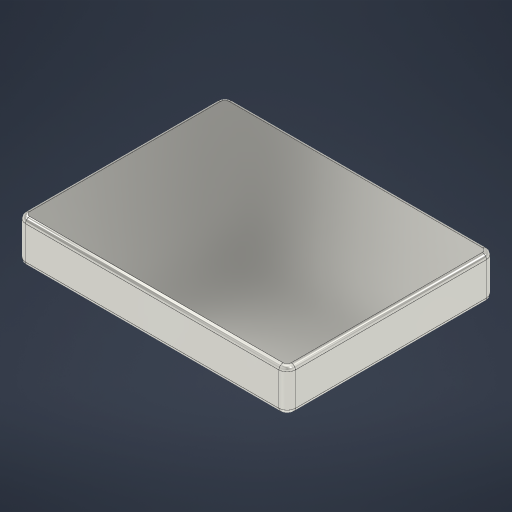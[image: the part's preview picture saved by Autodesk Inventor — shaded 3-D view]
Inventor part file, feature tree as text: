
AUTODESK INVENTOR PART (.ipt)
format: ipt  version: 2024.2 (Build 282272000, 272)  size: 222,208 bytes
history: native  units: mm
features: extrude x1, fillet x1, sketch x1, other x1
ambient origin geometry x8: Origin, YZ Plane, XZ Plane, XY Plane, X Axis, Y Axis, Z Axis, Center Point
bodies: Solid1 (feature_tree)
feature tree (4):
  extrude  "Extrusion1"  Depth=25.0mm
  fillet  "Fillet1"  Radius=1.0mm
  sketch  "Sketch1"  dims[d0=32.5mm d1=25.0mm d2=1.0mm d3=5.0mm d4=0.0mm d5=0.5mm]
  other  "Finish1"
